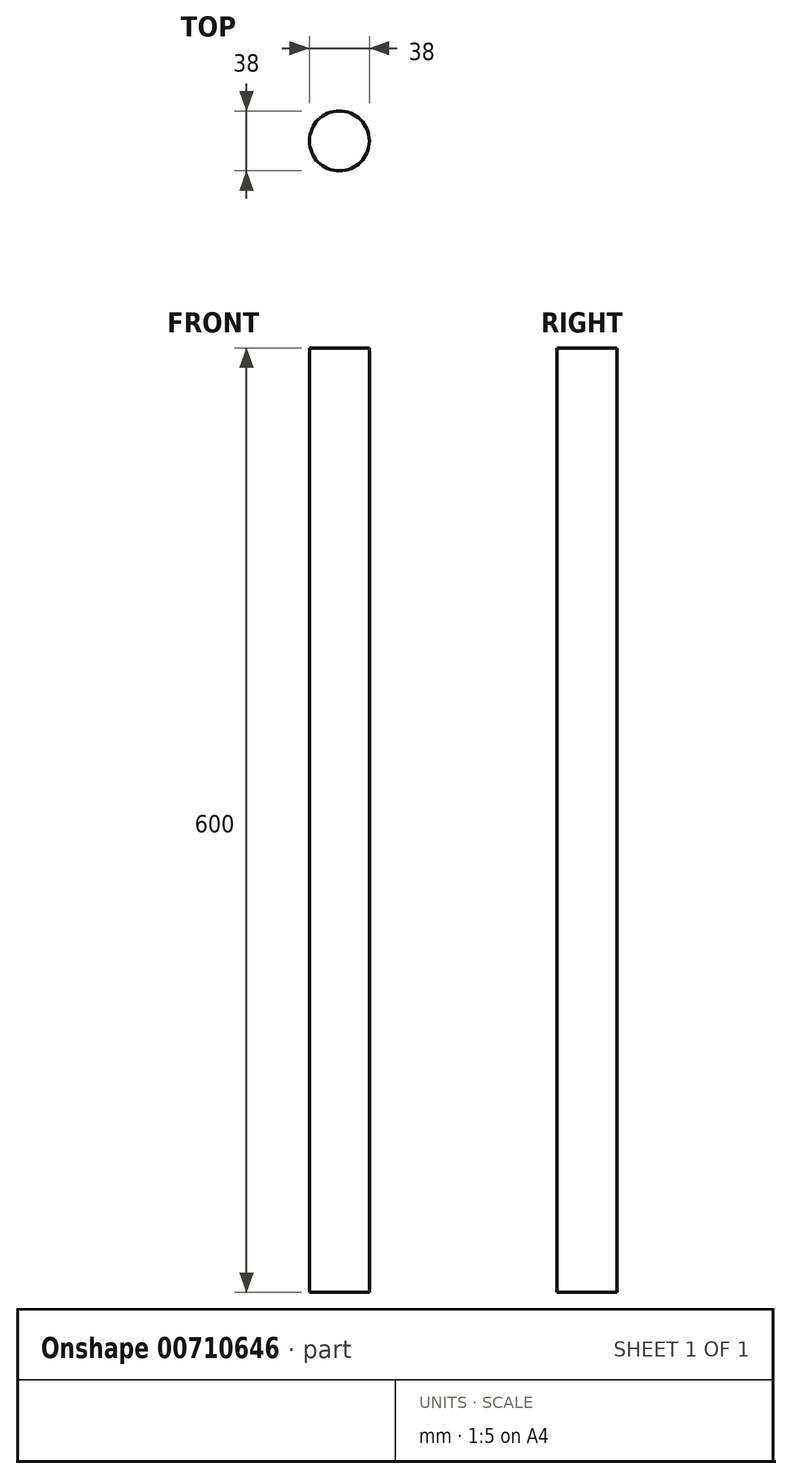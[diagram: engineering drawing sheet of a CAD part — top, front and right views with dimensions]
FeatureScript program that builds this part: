
annotation { "Feature Type Name" : "Feature", "Feature Type Description" : "" }
export const myFeature = defineFeature(function(context is Context, id is Id, definition is map)
    precondition{}
    {
        {
            var Q0;
            Q0=qCreatedBy(makeId("Top.planeOp"),FACE);
            var sketch = newSketch(context, id + "F0", { "sketchPlane" : qUnion([Q0])});
            skCircle(sketch, "E0", {"center": v(0, 0) * mm, "radius": 19 * mm});
            skSolve(sketch);
        }
        {
            var Q0;
            Q0=makeQuery(id+"F0.imprint","IMPRINT",FACE,{"disambiguationData":[TD([[makeQuery(id+"F0.imprint","IMPRINT",EDGE,{"derivedFrom":sQuery(id+"F0.wireOp",EDGE,"E0")}),1.0]])]});
            extrude(context, id + "F1", {"entities" : qUnion([Q0]), "depth" : 600 * mm, "offsetDistance" : 25 * mm});
        }
    });
